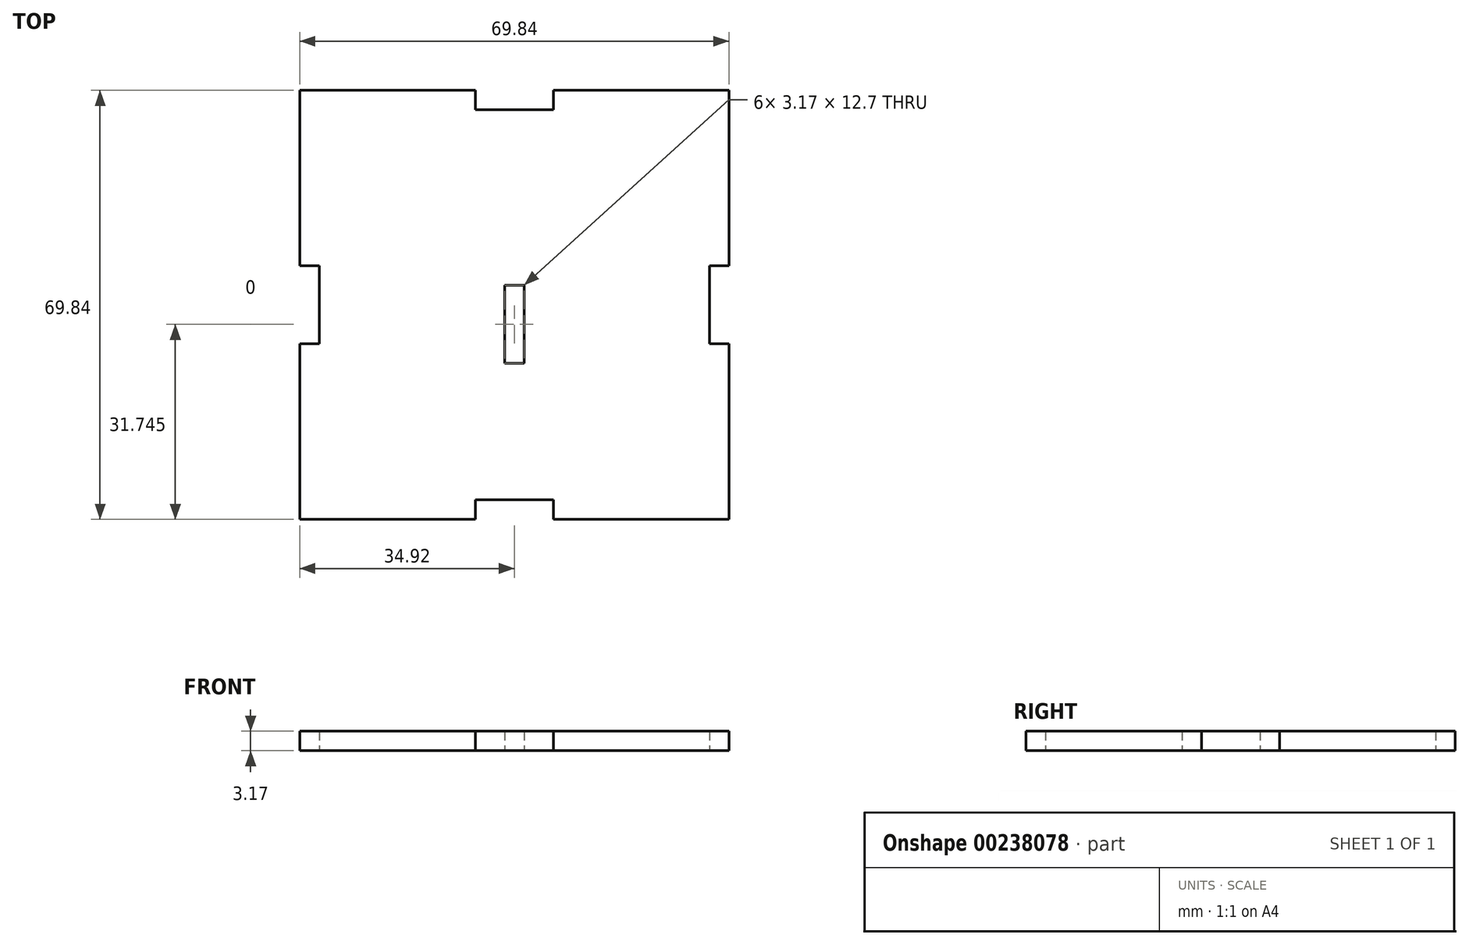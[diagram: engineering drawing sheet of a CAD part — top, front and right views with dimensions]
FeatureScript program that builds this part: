
annotation { "Feature Type Name" : "Feature", "Feature Type Description" : "" }
export const myFeature = defineFeature(function(context is Context, id is Id, definition is map)
    precondition{}
    {
        {
            var Q0;
            Q0=qCreatedBy(makeId("Top.planeOp"),FACE);
            var sketch = newSketch(context, id + "F0", { "sketchPlane" : qUnion([Q0])});
            skLineSegment(sketch, "E0.bottom", {"start": v(34.93, 34.93) * mm, "end": v(-34.93, 34.93) * mm});
            skLineSegment(sketch, "E0.top", {"start": v(34.93, -34.93) * mm, "end": v(-34.93, -34.93) * mm});
            skLineSegment(sketch, "E0.left", {"start": v(34.93, 34.93) * mm, "end": v(34.93, -34.93) * mm});
            skLineSegment(sketch, "E0.right", {"start": v(-34.93, 34.93) * mm, "end": v(-34.93, -34.93) * mm});
            skPoint(sketch, "E0.middle", {"position": v(0, 0) * mm});
            skLineSegment(sketch, "E1.bottom", {"start": v(31.75, 6.35) * mm, "end": v(34.93, 6.35) * mm});
            skLineSegment(sketch, "E1.top", {"start": v(31.75, -6.35) * mm, "end": v(34.93, -6.35) * mm});
            skLineSegment(sketch, "E1.left", {"start": v(31.75, 6.35) * mm, "end": v(31.75, -6.35) * mm});
            skLineSegment(sketch, "E1.right", {"start": v(34.93, 6.35) * mm, "end": v(34.93, -6.35) * mm});
            skLineSegment(sketch, "E2.bottom", {"start": v(-6.35, -31.75) * mm, "end": v(6.35, -31.75) * mm});
            skLineSegment(sketch, "E2.top", {"start": v(-6.35, -34.93) * mm, "end": v(6.35, -34.93) * mm});
            skLineSegment(sketch, "E2.left", {"start": v(-6.35, -31.75) * mm, "end": v(-6.35, -34.93) * mm});
            skLineSegment(sketch, "E2.right", {"start": v(6.35, -31.75) * mm, "end": v(6.35, -34.93) * mm});
            skLineSegment(sketch, "E3.bottom", {"start": v(-34.93, 6.35) * mm, "end": v(-31.75, 6.35) * mm});
            skLineSegment(sketch, "E3.top", {"start": v(-34.92, -6.35) * mm, "end": v(-31.75, -6.35) * mm});
            skLineSegment(sketch, "E3.left", {"start": v(-34.93, 6.35) * mm, "end": v(-34.93, -6.35) * mm});
            skLineSegment(sketch, "E3.right", {"start": v(-31.75, 6.35) * mm, "end": v(-31.75, -6.35) * mm});
            skLineSegment(sketch, "E4.bottom", {"start": v(-6.35, 34.93) * mm, "end": v(6.35, 34.93) * mm});
            skLineSegment(sketch, "E4.top", {"start": v(-6.35, 31.75) * mm, "end": v(6.35, 31.75) * mm});
            skLineSegment(sketch, "E4.left", {"start": v(-6.35, 34.93) * mm, "end": v(-6.35, 31.75) * mm});
            skLineSegment(sketch, "E4.right", {"start": v(6.35, 34.93) * mm, "end": v(6.35, 31.75) * mm});
            skLineSegment(sketch, "E5.bottom", {"start": v(-1.59, 3.18) * mm, "end": v(1.59, 3.18) * mm});
            skLineSegment(sketch, "E5.top", {"start": v(-1.59, -9.52) * mm, "end": v(1.59, -9.52) * mm});
            skLineSegment(sketch, "E5.left", {"start": v(-1.59, 3.17) * mm, "end": v(-1.59, -9.53) * mm});
            skLineSegment(sketch, "E5.right", {"start": v(1.59, 3.17) * mm, "end": v(1.59, -9.53) * mm});
            skSolve(sketch);
        }
        {
            var Q0;
            {var subQ13=sQuery(id+"F0.wireOp",EDGE,"E1.bottom");Q0=makeQuery(id+"F0.imprint","IMPRINT",FACE,{"disambiguationData":[TD([[makeQuery(id+"F0.imprint","IMPRINT",EDGE,{"derivedFrom":subQ13}),1.0]])]});}
            extrude(context, id + "F1", {"entities" : qUnion([Q0]), "depth" : 3.17 * mm});
        }
    });
